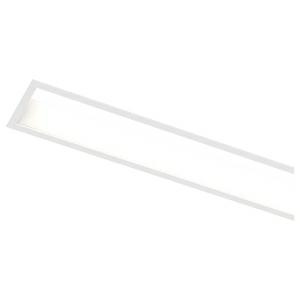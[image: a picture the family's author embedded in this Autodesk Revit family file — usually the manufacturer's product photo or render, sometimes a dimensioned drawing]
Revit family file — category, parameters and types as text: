
# Revit family: groove_l_1180_eb_led_21w_1364lm_3000k_cri80_230-2020_54a3
name_source: partatom
category: Leuchten
revit_build: Autodesk Revit 2016 (Build: 20190508_0715(x64)
units: mm (PartAtom-declared; Revit-internal decimal feet)

## family parameters
Basisbauteil = Fläche
Beim Laden mit Abzugskörper schneiden = Nein
Bemaßung runder Anschluss = Durchmesser verwenden
Gemeinsam genutzt = Nein
Lichtquelle = Nein
Raumberechnungspunkt = Nein
Teiletyp = Normal

## types (1)
- 230-2020- (4 x LED, 710 lm, 5.1 W, 3000K)
    Beschreibung = The recessed luminaire GROOVE from the familiy GROOVE consists of aluminum-extruded profile. Charming SOFT-EDGE design ensure unparalleled styling. The ballast is integrated and allows for an operation with 220-240V (50.60Hz). GROOVE (# 230-2020) ist not dimmable (on/off). The luminaire with direct illumination and corresponds to protection class SK1 at IP20.
    CIE Flux Codes = 59 87 97 100 49
    Color Rendering = 1B/80…89
    Color Temperature = 3000K
    Height = 0 mm  [stored 0 ft]
    Hersteller = Prolicht
    Lamp Light Flux = 710 lm
    Lamp Power = 5.1 W
    Lamp count = 4
    Lampe = 4 x LED
    Length = 1180 mm
    Luminous efficacy = 67 lm/W
    ModVariant = Nein
    Modell = 230-2020
    Mounting Place = Ceiling
    Mounting Type = Recessed
    Number of Poles = 1
    OnlyDefault = Ja
    Power Factor = 1
    Product Name = GROOVE L=1180 EB LED 21W 1364lm 3000K CRI80
    Product group = Recessed profile lights
    ProductGroupID = 423
    Protection Class = Protection class
    Protection Degree = Degree of protection
    RLX_Detail_Level = 1
    RlxData = <blob elided: 170373 chars, md5=29bddb06>
    Scheinlast = 20 VA
    Socket = socket
    Standby Power = 0 W
    System Light Flux = 1370 lm
    System Power = 20 W
    Typenbild = 230-2020.jpg
    URL = http://relux.com
    VarID = 230-2020-
    Voltage = 0 V
    Vorgabe-Ansicht = 1800 mm
    Weight = 0.00 kg
    Width = 92 mm

note: [stored X ft] marks values corroborated as IEEE doubles in the binary element streams (Revit-internal decimal feet)

## geometry (parser evidence)
native form markers: Sweep x15
no freeform markers — native parametric forms only
